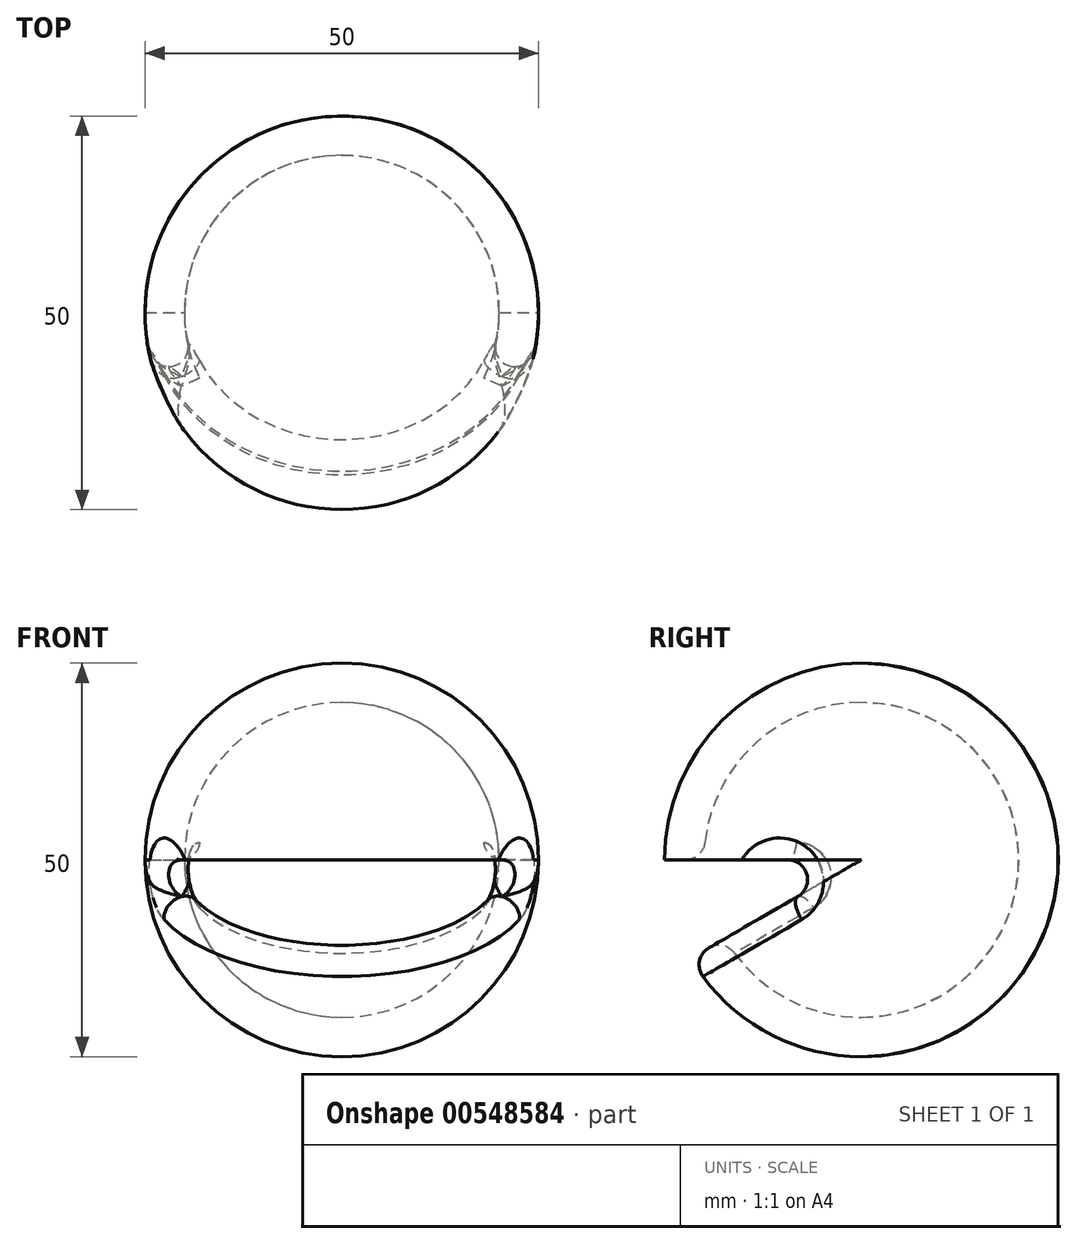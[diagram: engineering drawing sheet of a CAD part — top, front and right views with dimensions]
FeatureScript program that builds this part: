
annotation { "Feature Type Name" : "Feature", "Feature Type Description" : "" }
export const myFeature = defineFeature(function(context is Context, id is Id, definition is map)
    precondition{}
    {
        {
            var Q0;
            Q0=qCreatedBy(makeId("Front.planeOp"),FACE);
            var sketch = newSketch(context, id + "F0", { "sketchPlane" : qUnion([Q0])});
            skCircle(sketch, "E0", {"center": v(0, 0) * mm, "radius": 25 * mm});
            skLineSegment(sketch, "E1", {"start": v(0, 25) * mm, "end": v(0, -25) * mm});
            skSolve(sketch);
        }
        {
            var Q0;
            {var subQ0=sQuery(id+"F0.wireOp",EDGE,"E1");Q0=makeQuery(id+"F0.imprint","IMPRINT",FACE,{"disambiguationData":[TD([[makeQuery(id+"F0.imprint","IMPRINT",EDGE,{"derivedFrom":subQ0}),1.0]])]});}
            var Q1;
            Q1=sQuery(id+"F0.wireOp",EDGE,"E1");
            revolve(context, id + "F1", {"entities" : qUnion([Q0]), "axis" : qUnion([Q1]), "revolveType" : RevolveType.FULL});
        }
        {
            var Q0;
            {var subQ0=sQuery(id+"F0.wireOp",EDGE,"E1");Q0=makeQuery(id+"F0.imprint","IMPRINT",FACE,{"disambiguationData":[TD([[makeQuery(id+"F0.imprint","IMPRINT",EDGE,{"derivedFrom":subQ0}),1.0]])]});}
            var sketch = newSketch(context, id + "F2", { "sketchPlane" : qUnion([Q0])});
            skCircle(sketch, "E2", {"center": v(0, 0) * mm, "radius": 20 * mm});
            skSolve(sketch);
        }
        {
            var Q0;
            {var subQ0=sQuery(id+"F2.wireOp",EDGE,"E2");var subQ1=makeQuery(id+"F0.imprint","IMPRINT",EDGE,{"derivedFrom":sQuery(id+"F0.wireOp",EDGE,"E1")});var subQ2=makeQuery(id+"F2.imprint","INTERSECT",VERTEX,{"disambiguationData":[OD(0.0)],"derivedFrom":[subQ1,subQ0]});Q0=makeQuery(id+"F2.imprint","IMPRINT",FACE,{"disambiguationData":[TD([[makeQuery(id+"F2.imprint","IMPRINT",EDGE,{"disambiguationData":[TD([[subQ2,-1.0]])],"derivedFrom":subQ0}),1.0]])]});}
            var Q1;
            Q1=sQuery(id+"F0.wireOp",EDGE,"E1");
            revolve(context, id + "F3", {"operationType" : NewBodyOperationType.REMOVE, "entities" : qUnion([Q0]), "axis" : qUnion([Q1]), "revolveType" : RevolveType.FULL});
        }
        {
            var Q0;
            Q0=qCreatedBy(makeId("Top.planeOp"),FACE);
            var sketch = newSketch(context, id + "F4", { "sketchPlane" : qUnion([Q0])});
            skCircle(sketch, "E3", {"center": v(0, 0) * mm, "radius": 25 * mm});
            skLineSegment(sketch, "E4", {"start": v(-25, 0) * mm, "end": v(25, 0) * mm});
            skSolve(sketch);
        }
        {
            var Q0;
            {var subQ0=sQuery(id+"F4.wireOp",EDGE,"E4");Q0=makeQuery(id+"F4.imprint","IMPRINT",FACE,{"disambiguationData":[TD([[makeQuery(id+"F4.imprint","IMPRINT",EDGE,{"derivedFrom":subQ0}),-1.0]])]});}
            var Q1;
            Q1=sQuery(id+"F4.wireOp",EDGE,"E4");
            revolve(context, id + "F5", {"operationType" : NewBodyOperationType.REMOVE, "entities" : qUnion([Q0]), "axis" : qUnion([Q1]), "revolveType" : RevolveType.ONE_DIRECTION, "angle" : 30 * degree});
        }
        {
            var Q0;
            Q0=makeQuery(id+"F5.boolean.opBoolean","COPY",EDGE,{"derivedFrom":makeQuery(id+"F5.opRevolve","CAP_EDGE",EDGE,{"disambiguationData":[OSD([sQuery(id+"F4.wireOp",EDGE,"E3")])],"isStart":true})});
            var Q1;
            Q1=makeQuery(id+"F5.boolean.opBoolean","INTERSECT",EDGE,{"derivedFrom":[makeQuery(id+"F3.boolean.opBoolean","COPY",FACE,{"derivedFrom":makeQuery(id+"F3.opRevolve","SWEPT_FACE",FACE,{"disambiguationData":[OSD([sQuery(id+"F2.wireOp",EDGE,"E2")])]})}),makeQuery(id+"F5.opRevolve","CAP_FACE",FACE,{"disambiguationData":[OSD([sQuery(id+"F4.wireOp",EDGE,"E3"),sQuery(id+"F4.wireOp",EDGE,"E4")])],"isStart":true})]});
            var Q2;
            Q2=makeQuery(id+"F5.boolean.opBoolean","COPY",FACE,{"derivedFrom":makeQuery(id+"F5.opRevolve","CAP_FACE",FACE,{"disambiguationData":[OSD([sQuery(id+"F4.wireOp",EDGE,"E3"),sQuery(id+"F4.wireOp",EDGE,"E4")])],"isStart":false})});
            fillet(context, id + "F6", {"entities" : qUnion([Q0, Q1, Q2]), "radius" : 2.5 * mm, "tangentPropagation" : true, "allowEdgeOverflow" : false});
        }
    });
